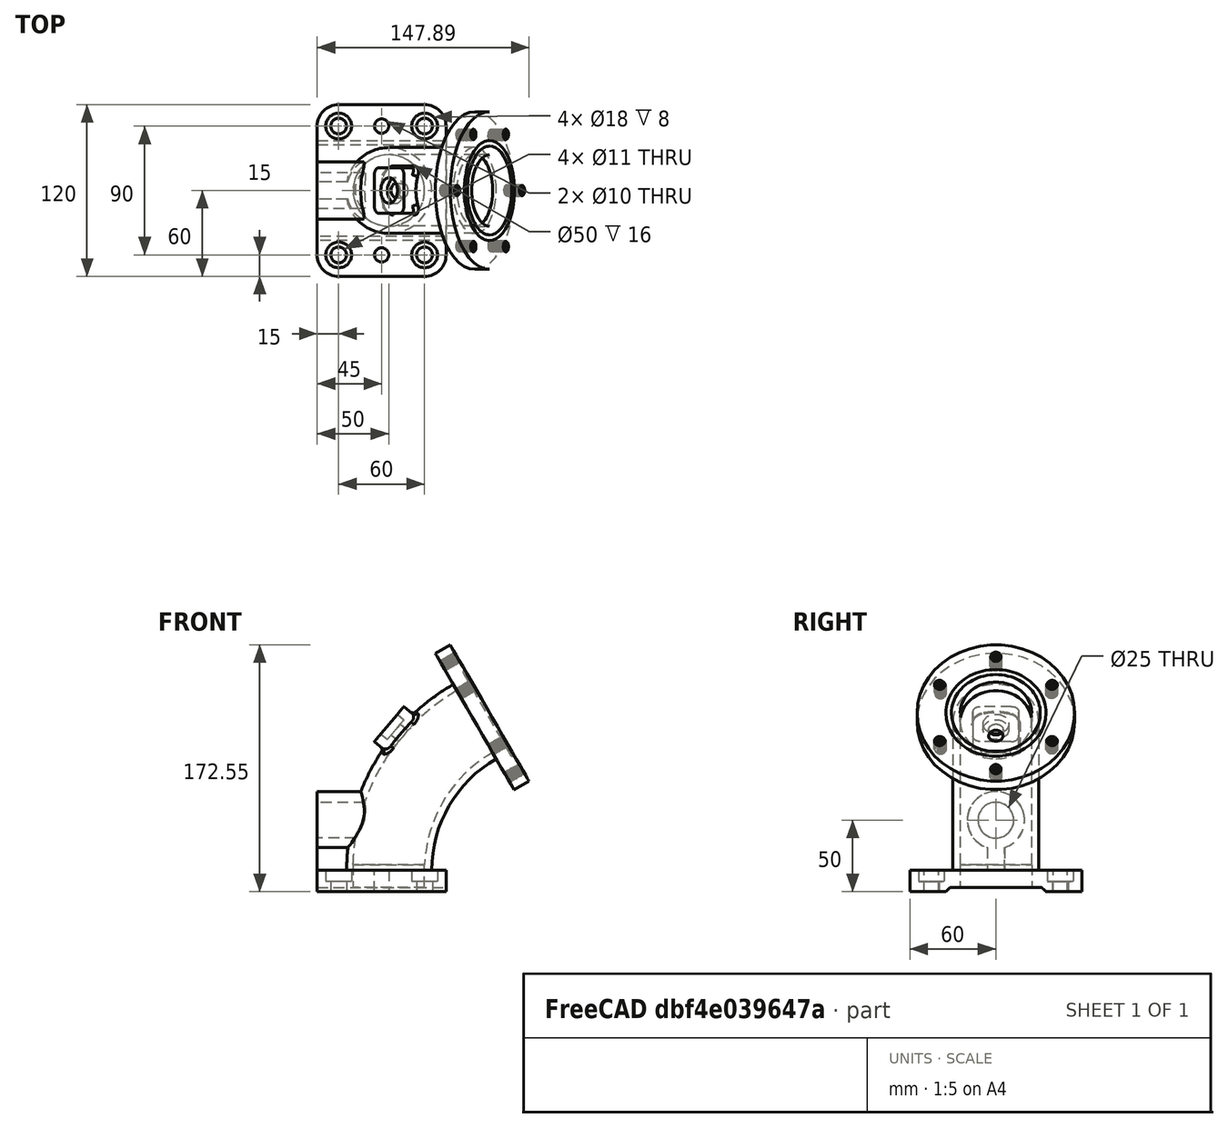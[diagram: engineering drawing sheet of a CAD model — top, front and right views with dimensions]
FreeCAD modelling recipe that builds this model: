
FCSTD DOCUMENT  (FreeCAD 0.21R33771 (Git))
Label: ex27
License: All rights reserved
LicenseURL: https://en.wikipedia.org/wiki/All_rights_reserved
objects: Sketcher::SketchObject×16, PartDesign::Pocket×5, PartDesign::Pad×4, PartDesign::Hole×3, PartDesign::SubtractivePipe×2, PartDesign::Fillet×2, PartDesign::AdditivePipe×1, PartDesign::Mirrored×1, PartDesign::PolarPattern×1, PartDesign::Groove×1, PartDesign::Body×1
note: 55 computed .brp shape members not serialized (recipe doc carries the construction recipe); baked Part::Feature solids carry a one-line shape summary decoded from their .brp

FEATURE [Sketcher::SketchObject] Sketch
  FullyConstrained = true
  MapMode = 5
  Placement = pos=(0,0,0) rot=(1,0,0;1.5708rad)
  Support = -> [XZ_Plane]
  sketch-geometry (2):
    g0: ArcOfCircle CenterX=120 CenterY=0 CenterZ=0 NormalX=0 NormalY=0 NormalZ=1 AngleXU=0 Radius=120 StartAngle=2.0944 EndAngle=3.14159
    g1: LineSegment StartX=60 StartY=103.923 StartZ=0 EndX=120 EndY=0 EndZ=0
  constraints (6):
    c: PointOnObject(g0,g-1)
    c: Coincident(g0,g-1)
    c: Coincident(g1,g0)
    c: Coincident(g1,g0)
    c: Angle(g1,g-1) = 1.0472
    c: Radius(g0) = 120
FEATURE [Sketcher::SketchObject] Sketch001
  FullyConstrained = true
  MapMode = 5
  Support = -> [XY_Plane]
  sketch-geometry (1):
    g0: Circle CenterX=0 CenterY=0 CenterZ=0 NormalX=0 NormalY=0 NormalZ=1 AngleXU=0 Radius=30
  constraints (2):
    c: Coincident(g0,g-1)
    c: Radius(g0) = 30
FEATURE [PartDesign::AdditivePipe] AdditivePipe
  AuxilleryCurvelinear = true
  AuxillerySpineTangent = false
  Binormal = (0,0,0)
  Mode = 0
  Profile = -> Sketch001
  Spine = -> Sketch
  SpineTangent = false
  Transformation = 0
  Transition = 0
FEATURE [Sketcher::SketchObject] Sketch002
  FullyConstrained = true
  MapMode = 5
  Support = -> [XY_Plane]
  sketch-geometry (10):
    g0: ArcOfCircle CenterX=-35 CenterY=45 CenterZ=0 NormalX=0 NormalY=0 NormalZ=1 AngleXU=0 Radius=15 StartAngle=1.5708 EndAngle=3.14159
    g1: LineSegment StartX=-35 StartY=60 StartZ=0 EndX=25 EndY=60 EndZ=0
    g2: ArcOfCircle CenterX=25 CenterY=45 CenterZ=0 NormalX=0 NormalY=0 NormalZ=1 AngleXU=0 Radius=15 StartAngle=1e-16 EndAngle=1.5708
    g3: LineSegment StartX=40 StartY=45 StartZ=0 EndX=40 EndY=-45 EndZ=0
    g4: ArcOfCircle CenterX=25 CenterY=-45 CenterZ=0 NormalX=0 NormalY=0 NormalZ=1 AngleXU=0 Radius=15 StartAngle=4.71239 EndAngle=6.28319
    g5: LineSegment StartX=25 StartY=-60 StartZ=0 EndX=-35 EndY=-60 EndZ=0
    g6: ArcOfCircle CenterX=-35 CenterY=-45 CenterZ=0 NormalX=0 NormalY=0 NormalZ=1 AngleXU=0 Radius=15 StartAngle=3.14159 EndAngle=4.71239
    g7: LineSegment StartX=-50 StartY=-45 StartZ=0 EndX=-50 EndY=45 EndZ=0
    g8: GeomPoint X=-50 Y=60 Z=0
    g9: GeomPoint X=40 Y=-60 Z=0
  constraints (23):
    c: Tangent(g0,g1) = 1.5708
    c: Tangent(g1,g2) = 1.5708
    c: Tangent(g2,g3) = 1.5708
    c: Tangent(g3,g4) = 1.5708
    c: Tangent(g4,g5) = 1.5708
    c: Tangent(g5,g6) = 1.5708
    c: Tangent(g6,g7) = 1.5708
    c: Tangent(g7,g0) = 1.5708
    c: Horizontal(g1)
    c: Horizontal(g5)
    c: Vertical(g3)
    c: Vertical(g7)
    c: Equal(g0,g2)
    c: Equal(g2,g4)
    c: PointOnObject(g8,g1)
    c: PointOnObject(g8,g7)
    c: PointOnObject(g9,g3)
    c: PointOnObject(g9,g5)
    c: Symmetric(g0,g6,g-1)
    c: Radius(g2) = 15
    c: DistanceX(g-1,g3) = 40
    c: DistanceX(g6,g3) = 90
    c: DistanceY(g5,g0) = 120
FEATURE [PartDesign::Pad] Pad
  BaseFeature = -> AdditivePipe
  Direction = (0,0,1)
  Length = 15
  Length2 = 10
  Profile = -> Sketch002
  ReferenceAxis = -> Sketch002 [N_Axis]
  Reversed = true
  Type = 0
FEATURE [Sketcher::SketchObject] Sketch003
  FullyConstrained = true
  MapMode = 5
  Placement = pos=(0,0,0) rot=(0.57735,0.57735,0.57735;2.0944rad)
  Support = -> [YZ_Plane]
  sketch-geometry (5):
    g0: ArcOfCircle CenterX=0 CenterY=35 CenterZ=0 NormalX=0 NormalY=0 NormalZ=1 AngleXU=0 Radius=20 StartAngle=5.01708 EndAngle=10.6909
    g1: LineSegment StartX=-6 StartY=15.9212 StartZ=0 EndX=6 EndY=15.9212 EndZ=0
    g2: LineSegment StartX=6 StartY=15.9212 StartZ=0 EndX=6 EndY=0 EndZ=0
    g3: LineSegment StartX=6 StartY=0 StartZ=0 EndX=-6 EndY=0 EndZ=0
    g4: LineSegment StartX=-6 StartY=0 StartZ=0 EndX=-6 EndY=15.9212 EndZ=0
  constraints (14):
    c: PointOnObject(g0,g-2)
    c: Coincident(g1,g2)
    c: Coincident(g2,g3)
    c: Coincident(g3,g4)
    c: Coincident(g4,g1)
    c: Horizontal(g1)
    c: Vertical(g2)
    c: PointOnObject(g2,g-1)
    c: Symmetric(g3,g2,g-2)
    c: Radius(g0) = 20
    c: DistanceX(g3,g3) = 12
    c: DistanceY(g2,g0) = 35
    c: Coincident(g0,g1)
    c: Coincident(g0,g1)
FEATURE [PartDesign::Pad] Pad001
  BaseFeature = -> Pad
  Direction = (1,-2e-16,3e-16)
  Length = 10
  Length2 = 10
  Profile = -> Sketch003
  ReferenceAxis = -> Sketch003 [N_Axis]
  Type = 3
  UpToFace = -> Pad [Face3]
FEATURE [Sketcher::SketchObject] Sketch004
  ExternalGeometry = -> [Pad001]
  FullyConstrained = true
  MapMode = 5
  Placement = pos=(90,-8.7e-15,51.9615) rot=(0.447214,0.447214,0.774597;1.82348rad)
  Support = -> [Pad001]
  sketch-geometry (1):
    g0: Circle CenterX=0 CenterY=60 CenterZ=0 NormalX=0 NormalY=0 NormalZ=1 AngleXU=0 Radius=55
  constraints (2):
    c: Coincident(g0,g-3)
    c: Radius(g0) = 55
FEATURE [PartDesign::Pad] Pad002
  BaseFeature = -> Pad001
  Direction = (0.866025,-1e-16,0.5)
  Length = 12
  Length2 = 10
  Profile = -> Sketch004
  ReferenceAxis = -> Sketch004 [N_Axis]
  Type = 0
FEATURE [Sketcher::SketchObject] Sketch005
  FullyConstrained = false
  MapMode = 5
  Placement = pos=(0,0,-15) rot=(1,0,0;3.14159rad)
  Support = -> [Pad002]
  sketch-geometry (5):
    g0: LineSegment StartX=-58.2201 StartY=35 StartZ=0 EndX=-58.2201 EndY=-35 EndZ=0
    g1: LineSegment StartX=-58.2201 StartY=-35 StartZ=0 EndX=58.2201 EndY=-35 EndZ=0
    g2: LineSegment StartX=58.2201 StartY=-35 StartZ=0 EndX=58.2201 EndY=35 EndZ=0
    g3: LineSegment StartX=58.2201 StartY=35 StartZ=0 EndX=-58.2201 EndY=35 EndZ=0
    g4: GeomPoint X=0 Y=0 Z=0
  constraints (11):
    c: Coincident(g0,g1)
    c: Coincident(g1,g2)
    c: Coincident(g2,g3)
    c: Coincident(g3,g0)
    c: Horizontal(g1)
    c: Horizontal(g3)
    c: Vertical(g0)
    c: Vertical(g2)
    c: Symmetric(g1,g0,g4)
    c: Coincident(g4,g-1)
    c: DistanceY(g2,g2) = 70
FEATURE [PartDesign::Pocket] Pocket
  BaseFeature = -> Pad002
  Direction = (0,0,1)
  Length = 3
  Length2 = 5
  Profile = -> Sketch005
  ReferenceAxis = -> Sketch005 [N_Axis]
  TaperAngle = -45
  Type = 0
FEATURE [Sketcher::SketchObject] Sketch006
  ExternalGeometry = -> [Pocket]
  FullyConstrained = false
  MapMode = 5
  Support = -> [Pocket]
  sketch-geometry (4):
    g0: Circle CenterX=-35 CenterY=45 CenterZ=0 NormalX=0 NormalY=0 NormalZ=1 AngleXU=0 Radius=8.22526
    g1: Circle CenterX=25 CenterY=45 CenterZ=0 NormalX=0 NormalY=0 NormalZ=1 AngleXU=0 Radius=8.22526
    g2: Circle CenterX=-35 CenterY=-45 CenterZ=0 NormalX=0 NormalY=0 NormalZ=1 AngleXU=0 Radius=8.22526
    g3: Circle CenterX=25 CenterY=-45 CenterZ=0 NormalX=0 NormalY=0 NormalZ=1 AngleXU=0 Radius=8.22526
  constraints (7):
    c: Coincident(g0,g-3)
    c: Coincident(g1,g-4)
    c: Coincident(g2,g-5)
    c: Coincident(g3,g-6)
    c: Equal(g3,g2)
    c: Equal(g2,g0)
    c: Equal(g0,g1)
FEATURE [PartDesign::Hole] Hole
  BaseFeature = -> Pocket
  CustomThreadClearance = 0
  Depth = 25
  DepthType = 0
  Diameter = 11
  DrillForDepth = false
  DrillPoint = 1
  DrillPointAngle = 118
  HoleCutCountersinkAngle = 90
  HoleCutCustomValues = false
  HoleCutDepth = 8
  HoleCutDiameter = 18
  HoleCutType = 1
  ModelThread = false
  Profile = -> Sketch006
  Tapered = false
  TaperedAngle = 90
  ThreadClass = 0
  ThreadDepth = 25
  ThreadDepthType = 0
  ThreadDirection = 0
  ThreadFit = 0
  ThreadSize = 0
  ThreadType = 0
  Threaded = false
  UseCustomThreadClearance = false
FEATURE [Sketcher::SketchObject] Sketch007
  ExternalGeometry = -> [Hole]
  FullyConstrained = true
  MapMode = 5
  Support = -> [Hole]
  sketch-geometry (1):
    g0: Circle CenterX=-5 CenterY=45 CenterZ=0 NormalX=0 NormalY=0 NormalZ=1 AngleXU=0 Radius=5
  constraints (2):
    c: Symmetric(g-4,g-5,g0)
    c: Radius(g0) = 5
FEATURE [PartDesign::Pocket] Pocket001
  BaseFeature = -> Hole
  Direction = (0,0,-1)
  Length = 16
  Length2 = 5
  Profile = -> Sketch007
  ReferenceAxis = -> Sketch007 [N_Axis]
  Type = 0
FEATURE [PartDesign::Mirrored] Mirrored
  BaseFeature = -> Pocket001
  MirrorPlane = -> XZ_Plane
  Originals = -> [Pocket001]
FEATURE [Sketcher::SketchObject] Sketch008
  ExternalGeometry = -> [Mirrored]
  FullyConstrained = false
  MapMode = 5
  Placement = pos=(100.392,-1.86e-14,57.9615) rot=(0.447214,0.447214,0.774597;1.82348rad)
  Support = -> [Mirrored]
  sketch-geometry (1):
    g0: Circle CenterX=0 CenterY=105 CenterZ=0 NormalX=0 NormalY=0 NormalZ=1 AngleXU=0 Radius=5.49636
  constraints (1):
    c: PointOnObject(g0,g-2)
FEATURE [PartDesign::Hole] Hole001
  BaseFeature = -> Mirrored
  CustomThreadClearance = 0
  Depth = 25
  DepthType = 0
  Diameter = 6.828
  DrillForDepth = false
  DrillPoint = 1
  DrillPointAngle = 118
  HoleCutCountersinkAngle = 90
  HoleCutCustomValues = false
  HoleCutDepth = 0
  HoleCutDiameter = 6.1
  HoleCutType = 0
  ModelThread = true
  Profile = -> Sketch008
  Tapered = false
  TaperedAngle = 90
  ThreadClass = 0
  ThreadDepth = 25
  ThreadDepthType = 0
  ThreadDirection = 0
  ThreadFit = 0
  ThreadSize = 16
  ThreadType = 1
  Threaded = true
  UseCustomThreadClearance = false
FEATURE [PartDesign::PolarPattern] PolarPattern
  Angle = 360
  Axis = -> Hole001 [Edge3]
  BaseFeature = -> Hole001
  Occurrences = 6
  Originals = -> [Hole001]
FEATURE [Sketcher::SketchObject] Sketch009
  ExternalGeometry = -> [PolarPattern]
  FullyConstrained = true
  MapMode = 5
  Placement = pos=(0,0,0) rot=(1,0,0;1.5708rad)
  Support = -> [XZ_Plane]
  sketch-geometry (1):
    g0: Circle CenterX=53.8923 CenterY=138.502 CenterZ=0 NormalX=0 NormalY=0 NormalZ=1 AngleXU=0 Radius=2
  constraints (3):
    c: PointOnObject(g0,g-3)
    c: Distance(g0,g-3) = 22
    c: Radius(g0) = 2
FEATURE [PartDesign::Groove] Groove
  Angle = 360
  Axis = (0.866025,-2e-16,0.5)
  Base = (70.3923,-3.4e-15,109.923)
  BaseFeature = -> PolarPattern
  Profile = -> Sketch009
  ReferenceAxis = -> PolarPattern [Edge3]
FEATURE [Sketcher::SketchObject] Sketch010
  ExternalGeometry = -> [Groove]
  FullyConstrained = true
  MapMode = 5
  Placement = pos=(100.392,-1.86e-14,57.9615) rot=(0.447214,0.447214,0.774597;1.82348rad)
  Support = -> [Groove]
  sketch-geometry (1):
    g0: Circle CenterX=0 CenterY=60 CenterZ=0 NormalX=0 NormalY=0 NormalZ=1 AngleXU=0 Radius=25
  constraints (2):
    c: Coincident(g0,g-3)
    c: Radius(g0) = 25
FEATURE [PartDesign::Pocket] Pocket002
  BaseFeature = -> Groove
  Direction = (-0.866025,1e-16,-0.5)
  Length = 12
  Length2 = 5
  Profile = -> Sketch010
  ReferenceAxis = -> Sketch010 [N_Axis]
  Type = 0
FEATURE [Sketcher::SketchObject] Sketch011
  FullyConstrained = true
  MapMode = 5
  Placement = pos=(0,0,-12) rot=(1,0,0;3.14159rad)
  Support = -> [Pocket002]
  sketch-geometry (1):
    g0: Circle CenterX=0 CenterY=0 CenterZ=0 NormalX=0 NormalY=0 NormalZ=1 AngleXU=0 Radius=25
  constraints (2):
    c: Coincident(g0,g-1)
    c: Radius(g0) = 25
FEATURE [PartDesign::Pocket] Pocket003
  BaseFeature = -> Pocket002
  Direction = (0,0,1)
  Length = 16
  Length2 = 5
  Profile = -> Sketch011
  ReferenceAxis = -> Sketch011 [N_Axis]
  Type = 0
FEATURE [Sketcher::SketchObject] Sketch012
  ExternalGeometry = -> [Pocket003]
  FullyConstrained = false
  MapMode = 5
  Placement = pos=(90,-1.53e-14,51.9615) rot=(0.447214,0.447214,0.774597;1.82348rad)
  Support = -> [Pocket003]
  sketch-geometry (1):
    g0: Circle CenterX=-1.61e-14 CenterY=60 CenterZ=0 NormalX=0 NormalY=0 NormalZ=1 AngleXU=0 Radius=24.9142
  constraints (1):
    c: Tangent(g0,g-3) = 1.5708
FEATURE [PartDesign::SubtractivePipe] SubtractivePipe
  AuxilleryCurvelinear = true
  AuxillerySpineTangent = false
  BaseFeature = -> Pocket003
  Binormal = (0,0,0)
  Mode = 0
  Profile = -> Sketch012
  Spine = -> Sketch
  SpineTangent = false
  Transformation = 0
  Transition = 0
FEATURE [Sketcher::SketchObject] Sketch013
  ExternalGeometry = -> [SubtractivePipe]
  FullyConstrained = false
  MapMode = 5
  Placement = pos=(0,0,0) rot=(1,0,0;1.5708rad)
  Support = -> [XZ_Plane]
  sketch-geometry (5):
    g0: LineSegment StartX=122.041 StartY=0 StartZ=0 EndX=0.239856 EndY=102.203 EndZ=0
    g1: LineSegment StartX=10.5245 StartY=114.46 StartZ=0 EndX=-10.0447 EndY=89.9465 EndZ=0
    g2: LineSegment StartX=-10.0447 StartY=89.9465 StartZ=0 EndX=31.2067 EndY=55.3324 EndZ=0
    g3: LineSegment StartX=31.2067 StartY=55.3324 StartZ=0 EndX=51.776 EndY=79.8458 EndZ=0
    g4: LineSegment StartX=51.776 StartY=79.8458 StartZ=0 EndX=10.5245 EndY=114.46 EndZ=0
  constraints (14):
    c: PointOnObject(g0,g-1)
    c: Angle(g0,g-4) = -0.349066
    c: Coincident(g1,g2)
    c: Coincident(g2,g3)
    c: Coincident(g3,g4)
    c: Coincident(g4,g1)
    c: Parallel(g4,g2)
    c: Parallel(g3,g1)
    c: Perpendicular(g3,g0)
    c: Parallel(g4,g0)
    c: Distance(g1) = 32
    c: Distance(g0) = 159
    c: Symmetric(g1,g1,g0)
    c: Distance(g4) = 53.85
FEATURE [PartDesign::Pad] Pad003
  BaseFeature = -> SubtractivePipe
  Direction = (0,-1,2e-16)
  Length = 32
  Length2 = 10
  Midplane = true
  Profile = -> Sketch013
  ReferenceAxis = -> Sketch013 [N_Axis]
  Type = 0
FEATURE [PartDesign::Fillet] Fillet
  Base = -> Pad003 [Edge251,Edge246,Edge247,Edge250]
  BaseFeature = -> Pad003
  Radius = 5
  SupportTransform = false
  UseAllEdges = false
FEATURE [PartDesign::Fillet] Fillet001
  Base = -> Fillet [Edge5,Edge7,Edge8,Edge6,Edge4,Edge2,Edge1,Edge3]
  BaseFeature = -> Fillet
  Radius = 3
  SupportTransform = false
  UseAllEdges = false
FEATURE [PartDesign::SubtractivePipe] SubtractivePipe001
  AuxilleryCurvelinear = true
  AuxillerySpineTangent = false
  BaseFeature = -> Fillet001
  Binormal = (0,0,0)
  Mode = 0
  Profile = -> Sketch012
  Spine = -> Sketch
  SpineTangent = false
  Transformation = 0
  Transition = 0
FEATURE [Sketcher::SketchObject] Sketch014
  ExternalGeometry = -> [SubtractivePipe001]
  FullyConstrained = true
  MapMode = 5
  Placement = pos=(-50,0,0) rot=(0.57735,-0.57735,-0.57735;2.0944rad)
  Support = -> [SubtractivePipe001]
  sketch-geometry (1):
    g0: Circle CenterX=0 CenterY=35 CenterZ=0 NormalX=0 NormalY=0 NormalZ=1 AngleXU=0 Radius=12.5
  constraints (2):
    c: Coincident(g0,g-3)
    c: Radius(g0) = 12.5
FEATURE [PartDesign::Pocket] Pocket004
  BaseFeature = -> SubtractivePipe001
  Direction = (1,0,0)
  Length = 5
  Length2 = 5
  Profile = -> Sketch014
  ReferenceAxis = -> Sketch014 [N_Axis]
  Type = 2
FEATURE [Sketcher::SketchObject] Sketch015
  ExternalGeometry = -> [Pocket004]
  FullyConstrained = false
  MapMode = 5
  Placement = pos=(-50.1845,9.4e-15,42.1098) rot=(0.389282,-0.389282,-0.834817;1.75037rad)
  Support = -> [Pocket004]
  sketch-geometry (2):
    g0: Circle CenterX=0 CenterY=78.4464 CenterZ=0 NormalX=0 NormalY=0 NormalZ=1 AngleXU=0 Radius=8.20985
    g1: LineSegment StartX=11 StartY=89.4464 StartZ=0 EndX=-11 EndY=67.4464 EndZ=0
  constraints (4):
    c: PointOnObject(g0,g-2)
    c: Coincident(g1,g-3)
    c: Coincident(g1,g-5)
    c: PointOnObject(g0,g1)
FEATURE [PartDesign::Hole] Hole002
  BaseFeature = -> Pocket004
  CustomThreadClearance = 0
  Depth = 25
  DepthType = 0
  Diameter = 10
  DrillForDepth = false
  DrillPoint = 1
  DrillPointAngle = 118
  HoleCutCountersinkAngle = 90
  HoleCutCustomValues = false
  HoleCutDepth = 6
  HoleCutDiameter = 18
  HoleCutType = 1
  ModelThread = false
  Profile = -> Sketch015
  Tapered = false
  TaperedAngle = 90
  ThreadClass = 0
  ThreadDepth = 25
  ThreadDepthType = 0
  ThreadDirection = 0
  ThreadFit = 0
  ThreadSize = 0
  ThreadType = 0
  Threaded = false
  UseCustomThreadClearance = false
FEATURE [PartDesign::Body] Body
  Group = -> [Sketch,Sketch001,AdditivePipe,Sketch002,Pad,Sketch003,Pad001,Sketch004,Pad002,Sketch005,Pocket,Sketch006,Hole,Sketch007,Pocket001,Mirrored,Sketch008,Hole001,PolarPattern,Sketch009,Groove,Sketch010,Pocket002,Sketch011,Pocket003,Sketch012,SubtractivePipe,Sketch013,Pad003,Fillet,Fillet001,SubtractivePipe001,Sketch014,Pocket004,Sketch015,Hole002]
  Origin = -> Origin
  Tip = -> Hole002
